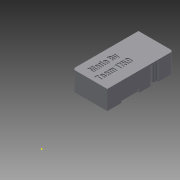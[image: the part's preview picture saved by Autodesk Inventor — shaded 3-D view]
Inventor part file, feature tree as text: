
AUTODESK INVENTOR PART (.ipt)
format: ipt  version: 2015 (Build 190159000, 159)  size: 570,368 bytes
history: native  units: in
note: dims shown in document units (in); Inventor stores cm internally (conversion verified against a paired STEP export)
features: extrude x10, sketch x9, projected_geometry x3, fillet x2, mirror x1
ambient origin geometry x8: Origin, YZ Plane, XZ Plane, XY Plane, X Axis, Y Axis, Z Axis, Center Point
bodies: Solid1 (feature_tree)
feature tree (25):
  extrude  "Extrusion1"  Depth=0.966in
  sketch  "Sketch2"  dims[d5=0.075in d6=0.1in d7=0.1in]
  fillet  "Fillet1"  Radius=0.533in
  fillet  "Fillet2"  Radius=0.075in
  extrude  "Extrusion2"  Depth=0.1in
  extrude  "Extrusion3"  Depth=0.125in
  extrude  "Extrusion4"  Depth=0.1in
  sketch  "Sketch6"  dims[d15=0.1in d16=0.1in]
  extrude  "Extrusion5"  Depth=0.1in
  sketch  "Sketch7"  dims[d17=0.1in d18=0.483in]
  extrude  "Extrusion7"  Depth=0.483in
  extrude  "Extrusion8"  Depth=0.1in
  extrude  "Extrusion9"  Depth=0.1in
  extrude  "Extrusion10"  Depth=0.5in
  mirror  "Mirror1"
  extrude  "Extrusion11"  Depth=0.45in
  sketch  "Sketch1"  dims[d0=1.833in d1=0.966in d2=0.533in d3=0.0in d4=0.075in]
  sketch  "Sketch4"  dims[d8=0.1in d9=0.1in d11=0.125in]
  sketch  "Sketch5"  dims[d13=0.175in d14=0.1in]
  sketch  "Sketch8"  dims[d19=0.0in d20=0.1in]
  projected_geometry  "Projected Loop1"
  sketch  "Sketch9"  dims[d21=0.24in d22=0.1in]
  projected_geometry  "Projected Loop2"
  sketch  "Sketch10"  dims[d23=0.535in d24=0.5in d25=0.45in d26=0.9in d27=0.533in d28=0.0in d29=0.279in d30=0.185in d32=0.3in d33=0.1in d34=0.533in d35=0.0in d36=0.1718in d37=1.2625in d38=0.025in d39=0.0in d40=0.05in d41=0.1in d42=0.025in d43=0.025in d46=0.05in d47=0.025in d48=0.0in d49=0.025in d50=0.0in d51=0.1in d52=0.5in d53=0.05in d54=0.0in d55=0.1in d56=0.0in d57=1.0in d58=0.5in d60=0.375in d61=0.025in d62=0.0in]
  projected_geometry  "Projected Loop3"
